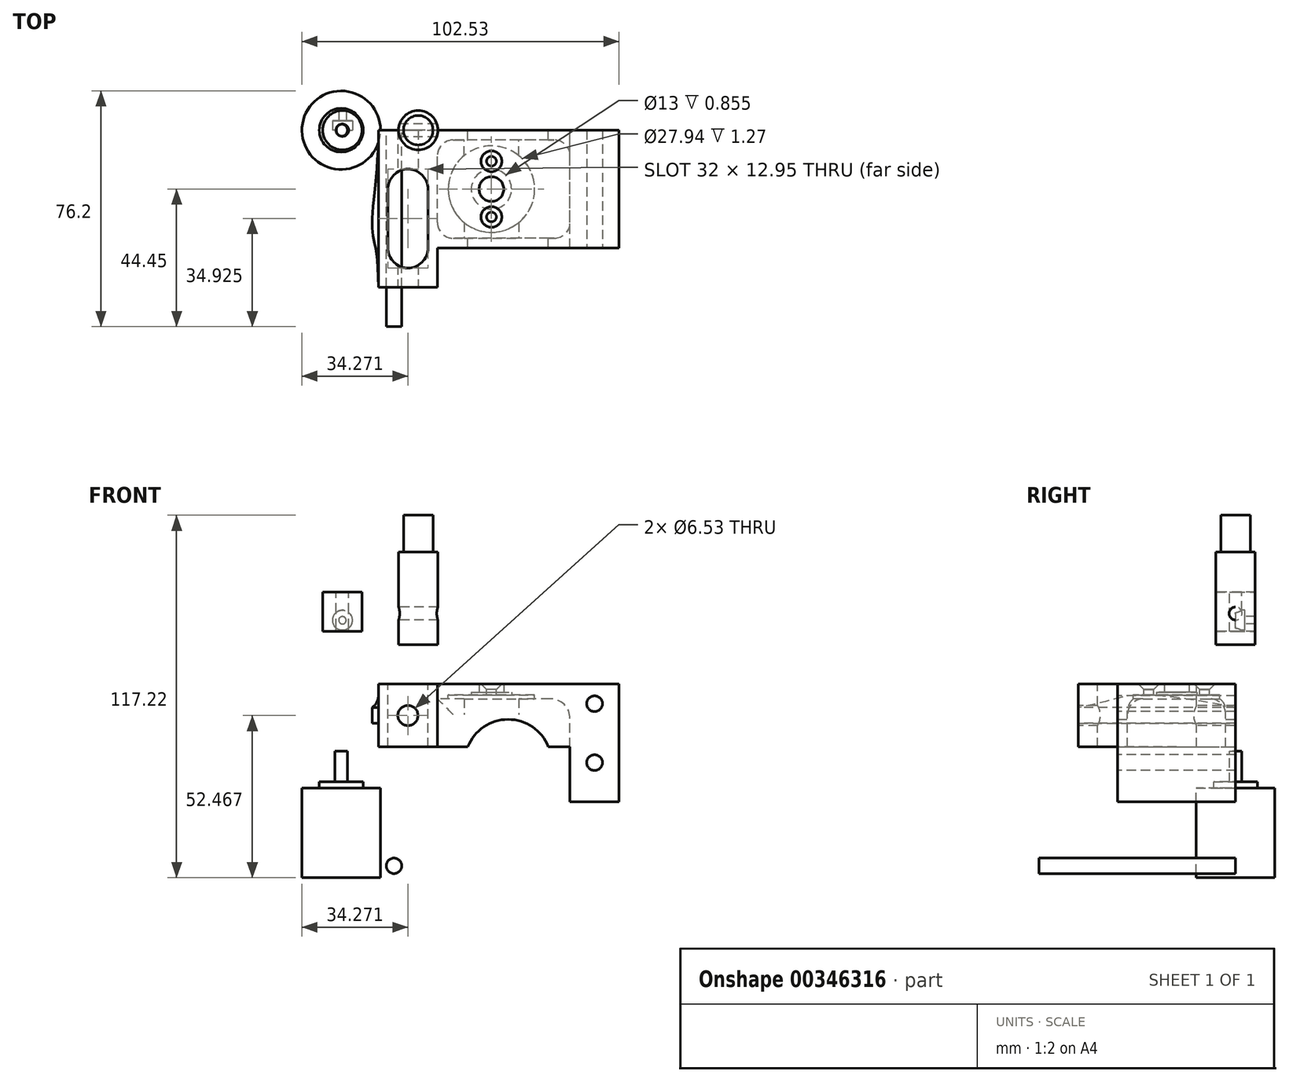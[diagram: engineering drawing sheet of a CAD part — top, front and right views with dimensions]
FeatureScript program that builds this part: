
annotation { "Feature Type Name" : "Feature", "Feature Type Description" : "" }
export const myFeature = defineFeature(function(context is Context, id is Id, definition is map)
    precondition{}
    {
        {
            var Q0;
            Q0=qCreatedBy(makeId("Top.planeOp"),FACE);
            var sketch = newSketch(context, id + "F0", { "sketchPlane" : qUnion([Q0])});
            skLineSegment(sketch, "E0.bottom", {"start": v(-76.2, 0) * mm, "end": v(76.2, 0) * mm});
            skLineSegment(sketch, "E0.top", {"start": v(-76.2, -76.2) * mm, "end": v(76.2, -76.2) * mm});
            skLineSegment(sketch, "E0.left", {"start": v(-76.2, 0) * mm, "end": v(-76.2, -76.2) * mm});
            skLineSegment(sketch, "E0.right", {"start": v(76.2, 0) * mm, "end": v(76.2, -76.2) * mm});
            skPoint(sketch, "E1", {"position": v(-44.45, -38.1) * mm});
            skSolve(sketch);
        }
        {
            var Q0;
            Q0=qCreatedBy(makeId("Front.planeOp"),FACE);
            var sketch = newSketch(context, id + "F1", { "sketchPlane" : qUnion([Q0])});
            skLineSegment(sketch, "E2.bottom", {"start": v(10.7, 46.54) * mm, "end": v(12.7, 46.54) * mm});
            skLineSegment(sketch, "E2.left", {"start": v(10.7, 46.54) * mm, "end": v(10.7, 36.54) * mm});
            skLineSegment(sketch, "E2.right", {"start": v(12.7, 46.54) * mm, "end": v(12.7, 34.54) * mm});
            skLineSegment(sketch, "E3.bottom", {"start": v(5.62, 34.54) * mm, "end": v(0, 34.54) * mm});
            skLineSegment(sketch, "E3.top", {"start": v(12.7, 5.54) * mm, "end": v(0, 5.54) * mm});
            skLineSegment(sketch, "E3.left", {"start": v(12.7, 34.54) * mm, "end": v(12.7, 5.54) * mm});
            skLineSegment(sketch, "E3.right", {"start": v(0, 34.54) * mm, "end": v(0, 5.54) * mm});
            skLineSegment(sketch, "E4.bottom", {"start": v(13.1, 85.18) * mm, "end": v(6.75, 85.18) * mm});
            skLineSegment(sketch, "E4.top", {"start": v(13.1, 97.88) * mm, "end": v(6.75, 97.88) * mm});
            skLineSegment(sketch, "E4.left", {"start": v(13.1, 85.18) * mm, "end": v(13.1, 97.88) * mm});
            skLineSegment(sketch, "E4.right", {"start": v(6.75, 85.18) * mm, "end": v(6.75, 97.88) * mm});
            skPoint(sketch, "E5", {"position": v(13.1, 52.41) * mm});
            skLineSegment(sketch, "E6", {"start": v(5.62, 36.54) * mm, "end": v(5.62, 34.54) * mm});
            skLineSegment(sketch, "E7", {"start": v(43.8, 68.17) * mm, "end": v(102.53, 68.17) * mm});
            skLineSegment(sketch, "E8", {"start": v(102.53, 68.17) * mm, "end": v(102.53, 30.07) * mm});
            skLineSegment(sketch, "E9", {"start": v(102.53, 30.07) * mm, "end": v(86.66, 30.07) * mm});
            skLineSegment(sketch, "E10", {"start": v(86.66, 30.07) * mm, "end": v(86.66, 57.05) * mm});
            skLineSegment(sketch, "E11", {"start": v(80.3, 63.4) * mm, "end": v(43.8, 63.4) * mm});
            skLineSegment(sketch, "E12", {"start": v(43.8, 63.4) * mm, "end": v(43.8, 68.17) * mm});
            skPoint(sketch, "E13.visualSharp", {"position": v(86.66, 63.4) * mm});
            skArc(sketch, "E13.filletArc", {"start": v(86.66, 57.05) * mm, "mid": v(84.8, 61.54) * mm, "end": v(80.3, 63.4) * mm});
            skLineSegment(sketch, "E14.bottom", {"start": v(43.8, 68.17) * mm, "end": v(24.75, 68.17) * mm});
            skLineSegment(sketch, "E14.top", {"start": v(43.8, 47.85) * mm, "end": v(24.75, 47.85) * mm});
            skLineSegment(sketch, "E14.left", {"start": v(43.8, 68.17) * mm, "end": v(43.8, 47.85) * mm});
            skLineSegment(sketch, "E14.right", {"start": v(24.75, 68.17) * mm, "end": v(24.75, 47.85) * mm});
            skLineSegment(sketch, "E15.bottom", {"start": v(32.84, 122.76) * mm, "end": v(37.6, 122.76) * mm});
            skLineSegment(sketch, "E15.top", {"start": v(31.26, 80.85) * mm, "end": v(37.6, 80.85) * mm});
            skLineSegment(sketch, "E15.left", {"start": v(31.26, 110.92) * mm, "end": v(31.26, 80.85) * mm});
            skLineSegment(sketch, "E15.right", {"start": v(37.6, 122.76) * mm, "end": v(37.6, 80.85) * mm});
            skLineSegment(sketch, "E16", {"start": v(5.62, 34.54) * mm, "end": v(5.62, 36.54) * mm});
            skLineSegment(sketch, "E17", {"start": v(5.62, 36.54) * mm, "end": v(10.7, 36.54) * mm});
            skCircle(sketch, "E18", {"center": v(29.75, 9.4) * mm, "radius": 2.5 * mm});
            skPoint(sketch, "E19", {"position": v(13.1, 88.8) * mm});
            skCircle(sketch, "E20", {"center": v(66.64, 42.77) * mm, "radius": 13.97 * mm});
            skLineSegment(sketch, "E21", {"start": v(32.84, 122.76) * mm, "end": v(32.84, 110.92) * mm});
            skLineSegment(sketch, "E22", {"start": v(32.84, 110.92) * mm, "end": v(31.26, 110.92) * mm});
            skSolve(sketch);
        }
        {
            var Q0;
            Q0=makeQuery(id+"F1.imprint","IMPRINT",FACE,{"disambiguationData":[TD([[makeQuery(id+"F1.imprint","IMPRINT",EDGE,{"derivedFrom":sQuery(id+"F1.wireOp",EDGE,"E2.bottom")}),-1.0]])]});
            var Q1;
            Q1=sQuery(id+"F1.wireOp",EDGE,"E2.right");
            revolve(context, id + "F2", {"entities" : qUnion([Q0]), "axis" : qUnion([Q1]), "revolveType" : RevolveType.FULL});
        }
        {
            var Q0;
            Q0=makeQuery(id+"F1.imprint","IMPRINT",FACE,{"disambiguationData":[TD([[makeQuery(id+"F1.imprint","IMPRINT",EDGE,{"derivedFrom":sQuery(id+"F1.wireOp",EDGE,"E4.bottom")}),-1.0]])]});
            var Q1;
            Q1=sQuery(id+"F1.wireOp",EDGE,"E4.left");
            revolve(context, id + "F3", {"entities" : qUnion([Q0]), "axis" : qUnion([Q1]), "revolveType" : RevolveType.FULL});
        }
        {
            var Q0;
            Q0=makeQuery(id+"F3.opRevolve","SWEPT_FACE",FACE,{"disambiguationData":[OSD([sQuery(id+"F1.wireOp",EDGE,"E4.top")])]});
            var sketch = newSketch(context, id + "F4", { "sketchPlane" : qUnion([Q0])});
            skPoint(sketch, "E23", {"position": v(13.1, 0) * mm});
            skSolve(sketch);
        }
        {
            var Q0;
            Q0=sQuery(id+"F4.wireOp",VERTEX,"E23");
            var Q1;
            Q1=makeQuery(id+"F3.opRevolve","SWEPT_BODY",BODY,{"disambiguationData":[OSD([sQuery(id+"F1.wireOp",EDGE,"E4.bottom"),sQuery(id+"F1.wireOp",EDGE,"E4.top"),sQuery(id+"F1.wireOp",EDGE,"E4.left"),sQuery(id+"F1.wireOp",EDGE,"E4.right")])]});
            hole(context, id + "F5", {"style" : HoleStyle.SIMPLE, "endStyle" : HoleEndStyle.THROUGH, "holeDiameter" : 4 * mm, "isTappedThrough" : true, "tappedDepth" : 12.7 * mm, "tapClearance" : 3, "locations" : qUnion([Q0]), "scope" : qUnion([Q1])});
        }
        {
            var Q0;
            Q0=makeQuery(id+"F1.imprint","IMPRINT",FACE,{"disambiguationData":[TD([[makeQuery(id+"F1.imprint","IMPRINT",EDGE,{"derivedFrom":sQuery(id+"F1.wireOp",EDGE,"E7")}),-1.0]])]});
            extrude(context, id + "F6", {"entities" : qUnion([Q0]), "depth" : 38.1 * mm});
        }
        {
            var Q0;
            Q0=makeQuery(id+"F6.opExtrude","SWEPT_FACE",FACE,{"disambiguationData":[OSD([sQuery(id+"F1.wireOp",EDGE,"E11")])]});
            var sketch = newSketch(context, id + "F7", { "sketchPlane" : qUnion([Q0])});
            skPoint(sketch, "E24", {"position": v(61.26, 19.05) * mm});
            skCircle(sketch, "E25", {"center": v(61.26, 19.05) * mm, "radius": 13.97 * mm, "construction": true});
            skCircle(sketch, "E26", {"center": v(61.26, 19.05) * mm, "radius": 13.97 * mm});
            skSolve(sketch);
        }
        {
            var Q0;
            Q0=sQuery(id+"F7.wireOp",VERTEX,"E24");
            var Q1;
            Q1=makeQuery(id+"F6.opExtrude","SWEPT_BODY",BODY,{"disambiguationData":[OSD([sQuery(id+"F1.wireOp",EDGE,"E7"),sQuery(id+"F1.wireOp",EDGE,"E8"),sQuery(id+"F1.wireOp",EDGE,"E9"),sQuery(id+"F1.wireOp",EDGE,"E10"),sQuery(id+"F1.wireOp",EDGE,"E11"),sQuery(id+"F1.wireOp",EDGE,"E12"),sQuery(id+"F1.wireOp",EDGE,"E13.filletArc")])]});
            hole(context, id + "F8", {"style" : HoleStyle.C_BORE, "endStyle" : HoleEndStyle.THROUGH, "standardTappedOrClearance" : lookupTablePath({ "standard" : "Custom", "fit" : "Normal", "size" : "M5", "type" : "Clearance" }), "standardBlindInLast" : lookupTablePath({ "fit" : "Standard", "standard" : "Custom", "size" : "M5", "type" : "Clearance" }), "holeDiameter" : 8 * mm, "cBoreDiameter" : 13 * mm, "cBoreDepth" : 2.12 * mm, "isTappedThrough" : true, "tappedDepth" : 12.7 * mm, "tapClearance" : 3, "locations" : qUnion([Q0]), "scope" : qUnion([Q1])});
        }
        {
            var Q0;
            Q0=makeQuery(id+"F6.opExtrude","SWEPT_FACE",FACE,{"disambiguationData":[OSD([sQuery(id+"F1.wireOp",EDGE,"E7")])]});
            var sketch = newSketch(context, id + "F9", { "sketchPlane" : qUnion([Q0])});
            skPoint(sketch, "E27", {"position": v(61.26, -19.05) * mm});
            skPoint(sketch, "E28", {"position": v(61.26, -28.05) * mm});
            skPoint(sketch, "E29", {"position": v(61.26, -10.05) * mm});
            skLineSegment(sketch, "E30.bottom", {"start": v(43.8, -38.1) * mm, "end": v(102.53, -38.1) * mm});
            skLineSegment(sketch, "E30.top", {"start": v(43.8, -34.92) * mm, "end": v(102.53, -34.92) * mm});
            skLineSegment(sketch, "E30.left", {"start": v(43.8, -38.1) * mm, "end": v(43.8, -34.92) * mm});
            skLineSegment(sketch, "E30.right", {"start": v(102.53, -38.1) * mm, "end": v(102.53, -34.92) * mm});
            skLineSegment(sketch, "E31.bottom", {"start": v(43.8, 0) * mm, "end": v(102.53, 0) * mm});
            skLineSegment(sketch, "E31.top", {"start": v(43.8, -3.17) * mm, "end": v(102.53, -3.17) * mm});
            skLineSegment(sketch, "E31.left", {"start": v(43.8, 0) * mm, "end": v(43.8, -3.17) * mm});
            skLineSegment(sketch, "E31.right", {"start": v(102.53, 0) * mm, "end": v(102.53, -3.17) * mm});
            skSolve(sketch);
        }
        {
            var Q0;
            Q0=sQuery(id+"F9.wireOp",VERTEX,"E29");
            var Q1;
            Q1=sQuery(id+"F9.wireOp",VERTEX,"E28");
            var Q2;
            Q2=makeQuery(id+"F6.opExtrude","SWEPT_BODY",BODY,{"disambiguationData":[OSD([sQuery(id+"F1.wireOp",EDGE,"E7"),sQuery(id+"F1.wireOp",EDGE,"E8"),sQuery(id+"F1.wireOp",EDGE,"E9"),sQuery(id+"F1.wireOp",EDGE,"E10"),sQuery(id+"F1.wireOp",EDGE,"E11"),sQuery(id+"F1.wireOp",EDGE,"E12"),sQuery(id+"F1.wireOp",EDGE,"E13.filletArc")])]});
            hole(context, id + "F10", {"style" : HoleStyle.C_SINK, "endStyle" : HoleEndStyle.THROUGH, "holeDiameter" : 3.15 * mm, "cSinkDiameter" : 6.72 * mm, "cSinkAngle" : 90 * degree, "isTappedThrough" : true, "tappedDepth" : 12.7 * mm, "tapClearance" : 3, "locations" : qUnion([Q0, Q1]), "scope" : qUnion([Q2])});
        }
        {
            var Q0;
            {var subQ3=sQuery(id+"F1.wireOp",EDGE,"E14.bottom");Q0=makeQuery(id+"F1.imprint","IMPRINT",FACE,{"disambiguationData":[TD([[makeQuery(id+"F1.imprint","IMPRINT",EDGE,{"derivedFrom":subQ3}),1.0]])]});}
            extrude(context, id + "F11", {"entities" : qUnion([Q0]), "operationType" : NewBodyOperationType.ADD, "depth" : 50.8 * mm});
        }
        {
            var Q0;
            Q0=makeQuery(id+"F11.boolean.opBoolean","MERGE",FACE,{"derivedFrom":[makeQuery(id+"F6.opExtrude","SWEPT_FACE",FACE,{"disambiguationData":[OSD([sQuery(id+"F1.wireOp",EDGE,"E7")])]}),makeQuery(id+"F11.opExtrude","SWEPT_FACE",FACE,{"disambiguationData":[OSD([sQuery(id+"F1.wireOp",EDGE,"E14.bottom")])]})]});
            var sketch = newSketch(context, id + "F12", { "sketchPlane" : qUnion([Q0])});
            skPoint(sketch, "E32", {"position": v(34.27, -19.05) * mm});
            skPoint(sketch, "E33", {"position": v(34.27, -38.1) * mm});
            skArc(sketch, "E34", {"start": v(40.75, -19.05) * mm, "mid": v(34.27, -12.57) * mm, "end": v(27.8, -19.05) * mm});
            skArc(sketch, "E35", {"start": v(27.8, -38.1) * mm, "mid": v(34.27, -44.58) * mm, "end": v(40.75, -38.1) * mm});
            skLineSegment(sketch, "E36", {"start": v(40.75, -38.1) * mm, "end": v(40.75, -19.05) * mm});
            skLineSegment(sketch, "E37", {"start": v(27.8, -38.1) * mm, "end": v(27.8, -19.05) * mm});
            skFitSpline(sketch, "E38", {"points": [v(24.75, 0) * mm, v(22.71, -31.42) * mm, v(24.75, -50.8) * mm], "startDerivative": vector(0, -77.17) * mm, "endDerivative": vector(0, -86.83) * mm});
            skSolve(sketch);
        }
        {
            var Q0;
            Q0=makeQuery(id+"F12.imprint","IMPRINT",FACE,{"disambiguationData":[TD([[makeQuery(id+"F12.imprint","IMPRINT",EDGE,{"derivedFrom":sQuery(id+"F12.wireOp",EDGE,"E34")}),1.0]])]});
            extrude(context, id + "F13", {"entities" : qUnion([Q0]), "operationType" : NewBodyOperationType.REMOVE, "endBound" : BoundingType.THROUGH_ALL, "oppositeDirection" : true, "depth" : 25.4 * mm});
        }
        {
            var Q0;
            Q0=makeQuery(id+"F11.opExtrude","CAP_FACE",FACE,{"disambiguationData":[OSD([sQuery(id+"F1.wireOp",EDGE,"E14.bottom"),sQuery(id+"F1.wireOp",EDGE,"E14.top"),sQuery(id+"F1.wireOp",EDGE,"E14.left"),sQuery(id+"F1.wireOp",EDGE,"E14.right")])],"isStart":false});
            var sketch = newSketch(context, id + "F14", { "sketchPlane" : qUnion([Q0])});
            skPoint(sketch, "E39", {"position": v(34.27, 58) * mm});
            skPoint(sketch, "E39.positionSnap0", {"position": v(43.8, 58) * mm});
            skPoint(sketch, "E39.positionSnap1", {"position": v(34.27, 47.85) * mm});
            skSolve(sketch);
        }
        {
            var Q0;
            Q0=sQuery(id+"F14.wireOp",VERTEX,"E39");
            var Q1;
            Q1=makeQuery(id+"F6.opExtrude","SWEPT_BODY",BODY,{"disambiguationData":[OSD([sQuery(id+"F1.wireOp",EDGE,"E7"),sQuery(id+"F1.wireOp",EDGE,"E8"),sQuery(id+"F1.wireOp",EDGE,"E9"),sQuery(id+"F1.wireOp",EDGE,"E10"),sQuery(id+"F1.wireOp",EDGE,"E11"),sQuery(id+"F1.wireOp",EDGE,"E13.filletArc"),sQuery(id+"F1.wireOp",EDGE,"E14.left")])]});
            hole(context, id + "F15", {"style" : HoleStyle.SIMPLE, "endStyle" : HoleEndStyle.THROUGH, "standardTappedOrClearance" : lookupTablePath({ "standard" : "ANSI", "fit" : "Close", "size" : "1/4", "type" : "Clearance" }), "standardBlindInLast" : lookupTablePath({ "fit" : "Close", "standard" : "ANSI", "size" : "1/4", "type" : "Clearance" }), "holeDiameter" : 6.53 * mm, "isTappedThrough" : true, "tappedDepth" : 12.7 * mm, "tapClearance" : 3, "locations" : qUnion([Q0]), "scope" : qUnion([Q1])});
        }
        {
            var Q0;
            Q0=makeQuery(id+"F1.imprint","IMPRINT",FACE,{"disambiguationData":[TD([[makeQuery(id+"F1.imprint","IMPRINT",EDGE,{"derivedFrom":sQuery(id+"F1.wireOp",EDGE,"E15.bottom")}),-1.0]])]});
            var Q1;
            Q1=sQuery(id+"F1.wireOp",EDGE,"E15.right");
            revolve(context, id + "F16", {"entities" : qUnion([Q0]), "axis" : qUnion([Q1]), "revolveType" : RevolveType.FULL});
        }
        {
            var Q0;
            Q0=qCreatedBy(makeId("Right.planeOp"),FACE);
            var sketch = newSketch(context, id + "F17", { "sketchPlane" : qUnion([Q0])});
            skPoint(sketch, "E40", {"position": v(0, 91) * mm});
            skSolve(sketch);
        }
        {
            var Q0;
            Q0=sQuery(id+"F17.wireOp",VERTEX,"E40");
            var Q1;
            Q1=makeQuery(id+"F16.opRevolve","SWEPT_BODY",BODY,{"disambiguationData":[OSD([sQuery(id+"F1.wireOp",EDGE,"E15.bottom"),sQuery(id+"F1.wireOp",EDGE,"E15.top"),sQuery(id+"F1.wireOp",EDGE,"E15.left"),sQuery(id+"F1.wireOp",EDGE,"E15.right")])]});
            hole(context, id + "F18", {"style" : HoleStyle.SIMPLE, "endStyle" : HoleEndStyle.THROUGH, "oppositeDirection" : true, "standardTappedOrClearance" : lookupTablePath({ "standard" : "ISO", "fit" : "Normal", "engagement" : "75%", "pitch" : "0.8 mm", "size" : "M5", "type" : "Tapped" }), "standardBlindInLast" : lookupTablePath({ "fit" : "Standard", "standard" : "ISO", "engagement" : "75%", "pitch" : "0.8 mm", "size" : "M5", "type" : "Tapped" }), "holeDiameter" : 4.2 * mm, "showTappedDepth" : true, "isTappedThrough" : true, "tappedDepth" : 12.7 * mm, "tapClearance" : 3, "locations" : qUnion([Q0]), "scope" : qUnion([Q1]), "majorDiameter" : 5 * mm});
        }
        {
            var Q0;
            Q0=makeQuery(id+"F9.imprint","IMPRINT",FACE,{"disambiguationData":[TD([[makeQuery(id+"F9.imprint","IMPRINT",EDGE,{"derivedFrom":sQuery(id+"F9.wireOp",EDGE,"E31.bottom")}),-1.0]])]});
            var Q1;
            Q1=makeQuery(id+"F9.imprint","IMPRINT",FACE,{"disambiguationData":[TD([[makeQuery(id+"F9.imprint","IMPRINT",EDGE,{"derivedFrom":sQuery(id+"F9.wireOp",EDGE,"E30.bottom")}),1.0]])]});
            extrude(context, id + "F19", {"entities" : qUnion([Q0, Q1]), "operationType" : NewBodyOperationType.ADD, "oppositeDirection" : true, "depth" : 20.32 * mm});
        }
        {
            var Q0;
            Q0=makeQuery(id+"F7.imprint","IMPRINT",FACE,{"disambiguationData":[TD([[makeQuery(id+"F7.imprint","IMPRINT",EDGE,{"derivedFrom":sQuery(id+"F7.wireOp",EDGE,"E26")}),1.0]])]});
            extrude(context, id + "F20", {"entities" : qUnion([Q0]), "operationType" : NewBodyOperationType.REMOVE, "depth" : 25.4 * mm, "hasSecondDirection" : true, "secondDirectionOppositeDirection" : true, "secondDirectionDepth" : 1.27 * mm});
        }
        {
            var Q0;
            Q0=makeQuery(id+"F1.imprint","IMPRINT",FACE,{"disambiguationData":[TD([[makeQuery(id+"F1.imprint","IMPRINT",EDGE,{"derivedFrom":sQuery(id+"F1.wireOp",EDGE,"E18")}),1.0]])]});
            extrude(context, id + "F21", {"entities" : qUnion([Q0]), "depth" : 63.5 * mm});
        }
        {
            var Q0;
            Q0=sQuery(id+"F1.wireOp",VERTEX,"E19");
            var Q1;
            Q1=makeQuery(id+"F3.opRevolve","SWEPT_BODY",BODY,{"disambiguationData":[OSD([sQuery(id+"F1.wireOp",EDGE,"E4.bottom"),sQuery(id+"F1.wireOp",EDGE,"E4.top"),sQuery(id+"F1.wireOp",EDGE,"E4.left"),sQuery(id+"F1.wireOp",EDGE,"E4.right")])]});
            hole(context, id + "F22", {"style" : HoleStyle.C_BORE, "endStyle" : HoleEndStyle.THROUGH, "standardTappedOrClearance" : lookupTablePath({ "standard" : "ISO", "engagement" : "75%", "pitch" : "0.6 mm", "size" : "M3", "type" : "Tapped" }), "standardBlindInLast" : lookupTablePath({ "standard" : "ISO", "engagement" : "75%", "pitch" : "0.6 mm", "size" : "M3", "type" : "Tapped" }), "holeDiameter" : 2.4 * mm, "cBoreDiameter" : 6.5 * mm, "cBoreDepth" : 3 * mm, "showTappedDepth" : true, "isTappedThrough" : true, "tappedDepth" : 12.7 * mm, "tapClearance" : 3, "locations" : qUnion([Q0]), "scope" : qUnion([Q1])});
        }
        {
            var Q0;
            Q0=makeQuery(id+"F12.imprint","IMPRINT",FACE,{"disambiguationData":[TD([[makeQuery(id+"F12.imprint","IMPRINT",EDGE,{"derivedFrom":sQuery(id+"F12.wireOp",EDGE,"E38")}),1.0]])]});
            extrude(context, id + "F23", {"entities" : qUnion([Q0]), "operationType" : NewBodyOperationType.ADD, "oppositeDirection" : true, "depth" : 12.7 * mm, "hasSecondDirection" : true, "secondDirectionOppositeDirection" : true, "secondDirectionDepth" : 7.62 * mm});
        }
        {
            var Q0;
            Q0=makeQuery(id+"F23.opExtrude","CAP_EDGE",EDGE,{"disambiguationData":[OSD([sQuery(id+"F1.wireOp",EDGE,"E14.bottom"),sQuery(id+"F1.wireOp",EDGE,"E14.right")])],"isStart":true});
            var Q1;
            Q1=makeQuery(id+"F23.opExtrude","CAP_EDGE",EDGE,{"disambiguationData":[OSD([sQuery(id+"F1.wireOp",EDGE,"E14.bottom"),sQuery(id+"F1.wireOp",EDGE,"E14.right")])],"isStart":false});
            fillet(context, id + "F24", {"entities" : qUnion([Q0, Q1]), "radius" : 5.08 * mm, "tangentPropagation" : true, "allowEdgeOverflow" : false});
        }
        {
            var Q0;
            Q0=makeQuery(id+"F1.imprint","IMPRINT",FACE,{"disambiguationData":[TD([[makeQuery(id+"F1.imprint","IMPRINT",EDGE,{"derivedFrom":sQuery(id+"F1.wireOp",EDGE,"E20")}),1.0]])]});
            extrude(context, id + "F25", {"entities" : qUnion([Q0]), "operationType" : NewBodyOperationType.REMOVE, "depth" : 50.8 * mm});
        }
        {
            var Q0;
            Q0=makeQuery(id+"F19.boolean.opBoolean","MERGE",FACE,{"derivedFrom":[makeQuery(id+"F6.opExtrude","CAP_FACE",FACE,{"disambiguationData":[OSD([sQuery(id+"F1.wireOp",EDGE,"E7"),sQuery(id+"F1.wireOp",EDGE,"E8"),sQuery(id+"F1.wireOp",EDGE,"E9"),sQuery(id+"F1.wireOp",EDGE,"E10"),sQuery(id+"F1.wireOp",EDGE,"E11"),sQuery(id+"F1.wireOp",EDGE,"E13.filletArc"),sQuery(id+"F1.wireOp",EDGE,"E14.left")])],"isStart":false}),makeQuery(id+"F19.opExtrude","SWEPT_FACE",FACE,{"disambiguationData":[OSD([sQuery(id+"F9.wireOp",EDGE,"E30.bottom")])]})]});
            var sketch = newSketch(context, id + "F26", { "sketchPlane" : qUnion([Q0])});
            skPoint(sketch, "E41", {"position": v(94.6, 61.82) * mm});
            skPoint(sketch, "E42", {"position": v(94.6, 42.77) * mm});
            skSolve(sketch);
        }
        {
            var Q0;
            Q0=sQuery(id+"F26.wireOp",VERTEX,"E41");
            var Q1;
            Q1=sQuery(id+"F26.wireOp",VERTEX,"E42");
            var Q2;
            Q2=makeQuery(id+"F6.opExtrude","SWEPT_BODY",BODY,{"disambiguationData":[OSD([sQuery(id+"F1.wireOp",EDGE,"E7"),sQuery(id+"F1.wireOp",EDGE,"E8"),sQuery(id+"F1.wireOp",EDGE,"E9"),sQuery(id+"F1.wireOp",EDGE,"E10"),sQuery(id+"F1.wireOp",EDGE,"E11"),sQuery(id+"F1.wireOp",EDGE,"E13.filletArc"),sQuery(id+"F1.wireOp",EDGE,"E14.left")])]});
            hole(context, id + "F27", {"style" : HoleStyle.SIMPLE, "endStyle" : HoleEndStyle.THROUGH, "standardTappedOrClearance" : lookupTablePath({ "standard" : "ANSI", "fit" : "Normal (ASME)", "size" : "#10", "type" : "Clearance" }), "standardBlindInLast" : lookupTablePath({ "fit" : "Free", "standard" : "ANSI", "size" : "#10", "type" : "Clearance" }), "holeDiameter" : 5.1 * mm, "isTappedThrough" : true, "tappedDepth" : 12.7 * mm, "tapClearance" : 3, "locations" : qUnion([Q0, Q1]), "scope" : qUnion([Q2])});
        }
        {
            var Q0;
            Q0=makeQuery(id+"F19.boolean.opBoolean","INTERSECT",EDGE,{"derivedFrom":[makeQuery(id+"F6.opExtrude","SWEPT_FACE",FACE,{"disambiguationData":[OSD([sQuery(id+"F1.wireOp",EDGE,"E11")])]}),makeQuery(id+"F19.opExtrude","SWEPT_FACE",FACE,{"disambiguationData":[OSD([sQuery(id+"F9.wireOp",EDGE,"E30.top")])]})]});
            var Q1;
            Q1=makeQuery(id+"F6.opExtrude","SWEPT_EDGE",EDGE,{"disambiguationData":[OSD([sQuery(id+"F1.wireOp",EDGE,"E11"),sQuery(id+"F1.wireOp",EDGE,"E14.left")])]});
            var Q2;
            Q2=makeQuery(id+"F19.opExtrude","SWEPT_EDGE",EDGE,{"disambiguationData":[OSD([sQuery(id+"F1.wireOp",EDGE,"E7"),sQuery(id+"F1.wireOp",EDGE,"E14.bottom"),sQuery(id+"F1.wireOp",EDGE,"E14.left"),sQuery(id+"F9.wireOp",EDGE,"E30.top"),sQuery(id+"F9.wireOp",EDGE,"E30.left")])]});
            var Q3;
            Q3=makeQuery(id+"F19.opExtrude","SWEPT_EDGE",EDGE,{"disambiguationData":[OSD([sQuery(id+"F1.wireOp",EDGE,"E7"),sQuery(id+"F1.wireOp",EDGE,"E14.bottom"),sQuery(id+"F1.wireOp",EDGE,"E14.left"),sQuery(id+"F9.wireOp",EDGE,"E31.top"),sQuery(id+"F9.wireOp",EDGE,"E31.left")])]});
            var Q4;
            Q4=makeQuery(id+"F19.boolean.opBoolean","INTERSECT",EDGE,{"derivedFrom":[makeQuery(id+"F6.opExtrude","SWEPT_FACE",FACE,{"disambiguationData":[OSD([sQuery(id+"F1.wireOp",EDGE,"E11")])]}),makeQuery(id+"F19.opExtrude","SWEPT_FACE",FACE,{"disambiguationData":[OSD([sQuery(id+"F9.wireOp",EDGE,"E31.top")])]})]});
            var Q5;
            Q5=makeQuery(id+"F19.boolean.opBoolean","MERGE",EDGE,{"derivedFrom":[makeQuery(id+"F6.opExtrude","CAP_EDGE",EDGE,{"disambiguationData":[OSD([sQuery(id+"F1.wireOp",EDGE,"E14.left")])],"isStart":false}),makeQuery(id+"F19.opExtrude","SWEPT_EDGE",EDGE,{"disambiguationData":[OSD([sQuery(id+"F9.wireOp",EDGE,"E30.bottom"),sQuery(id+"F9.wireOp",EDGE,"E30.left")])]})]});
            fillet(context, id + "F28", {"entities" : qUnion([Q0, Q1, Q2, Q3, Q4, Q5]), "radius" : 5.08 * mm, "tangentPropagation" : true, "allowEdgeOverflow" : false});
        }
    });
